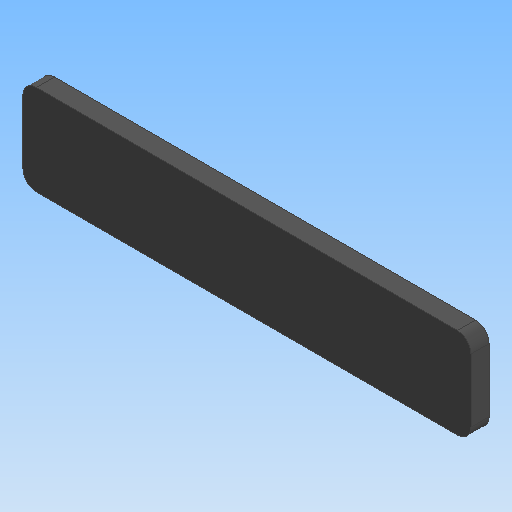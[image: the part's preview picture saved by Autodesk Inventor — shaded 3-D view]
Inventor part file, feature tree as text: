
AUTODESK INVENTOR PART (.ipt)
format: ipt  version: 2020 (Build 240168000, 168)  size: 117,248 bytes
history: native  units: mm
features: other x1, extrude x1
ambient origin geometry x8: Origin, YZ Plane, XZ Plane, XY Plane, X Axis, Y Axis, Z Axis, Center Point
bodies: Body1 (feature_tree)
feature tree (2):
  other  "實體1"
  extrude  "擠出1"  Depth=49.5mm
